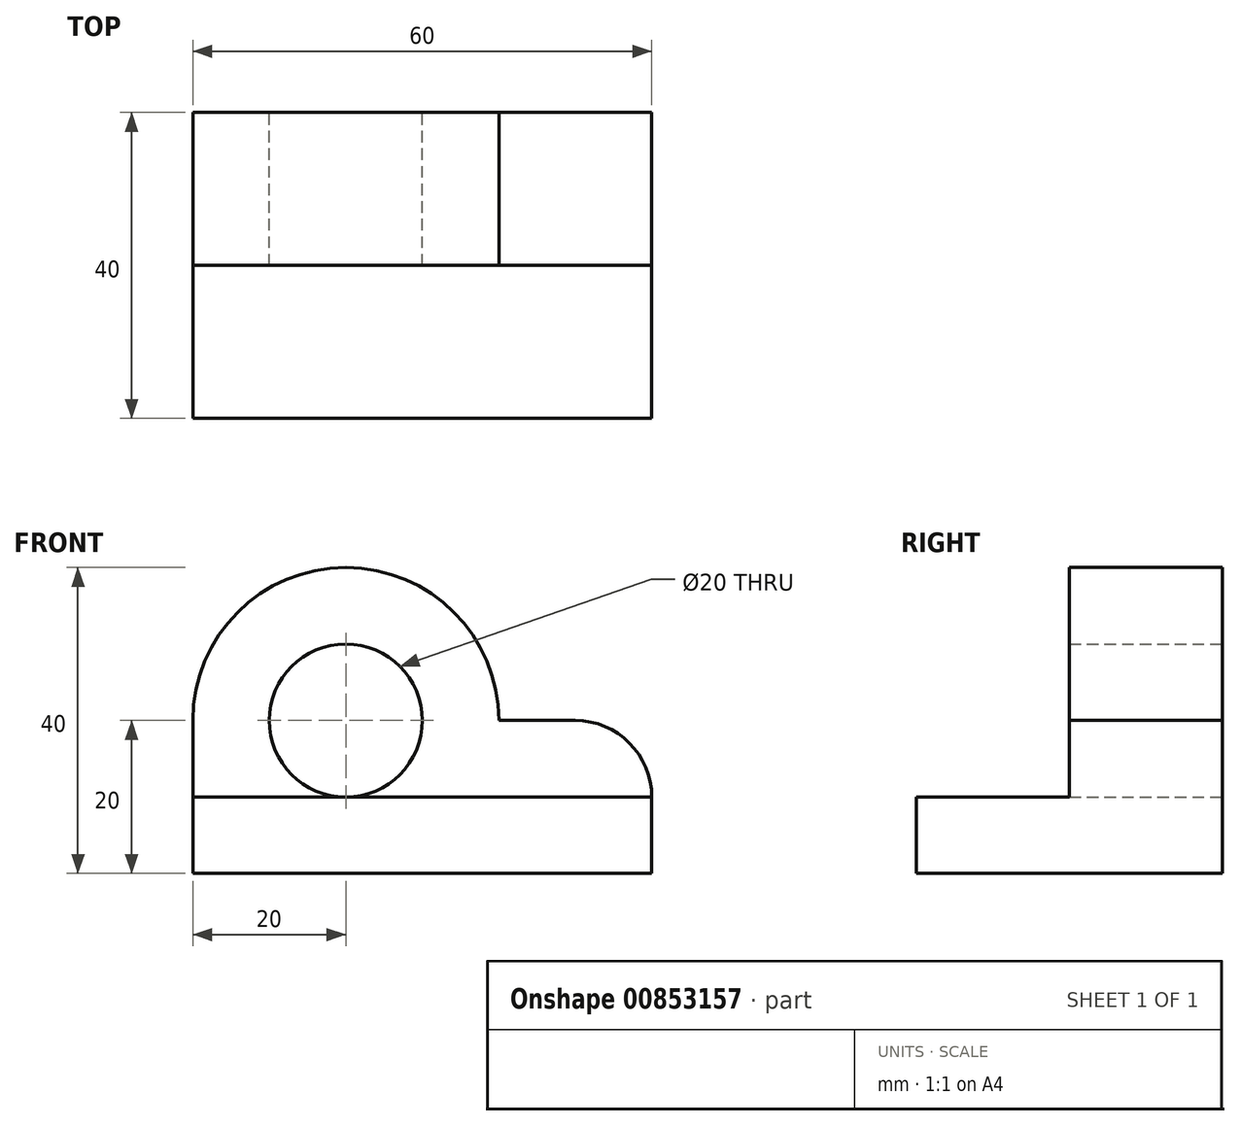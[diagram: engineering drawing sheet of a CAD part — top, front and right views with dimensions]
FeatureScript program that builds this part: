
annotation { "Feature Type Name" : "Feature", "Feature Type Description" : "" }
export const myFeature = defineFeature(function(context is Context, id is Id, definition is map)
    precondition{}
    {
        {
            var Q0;
            Q0=qCreatedBy(makeId("Front.planeOp"),FACE);
            var sketch = newSketch(context, id + "F0", { "sketchPlane" : qUnion([Q0])});
            skLineSegment(sketch, "E0", {"start": v(0, 0) * mm, "end": v(-60, 0) * mm});
            skLineSegment(sketch, "E1", {"start": v(-60, 0) * mm, "end": v(-60, 10) * mm});
            skLineSegment(sketch, "E2", {"start": v(0, 10) * mm, "end": v(0, 0) * mm});
            skArc(sketch, "E3", {"start": v(-20, 20) * mm, "mid": v(-40, 40) * mm, "end": v(-60, 20) * mm});
            skLineSegment(sketch, "E4", {"start": v(-60, 10) * mm, "end": v(-60, 20) * mm});
            skLineSegment(sketch, "E5", {"start": v(0, 10) * mm, "end": v(0, 10) * mm});
            skCircle(sketch, "E6", {"center": v(-40, 20) * mm, "radius": 10 * mm});
            skLineSegment(sketch, "E7", {"start": v(-10, 20) * mm, "end": v(-20, 20) * mm});
            skPoint(sketch, "E8.visualSharp", {"position": v(0, 20) * mm});
            skArc(sketch, "E8.filletArc", {"start": v(0, 10) * mm, "mid": v(-2.93, 17.07) * mm, "end": v(-10, 20) * mm});
            skSolve(sketch);
        }
        {
            var Q0;
            Q0 = qSketchRegion(id + "F0", true);
            extrude(context, id + "F1", {"entities" : qUnion([Q0]), "depth" : 20 * mm, "offsetDistance" : 25 * mm});
        }
        {
            var Q0;
            Q0=makeQuery(id+"F1.opExtrude","CAP_FACE",FACE,{"disambiguationData":[OSD([sQuery(id+"F0.wireOp",EDGE,"E0"),sQuery(id+"F0.wireOp",EDGE,"E1"),sQuery(id+"F0.wireOp",EDGE,"E2"),sQuery(id+"F0.wireOp",EDGE,"E3"),sQuery(id+"F0.wireOp",EDGE,"E4"),sQuery(id+"F0.wireOp",EDGE,"E6"),sQuery(id+"F0.wireOp",EDGE,"E7"),sQuery(id+"F0.wireOp",EDGE,"E8.filletArc")])],"isStart":false});
            var sketch = newSketch(context, id + "F2", { "sketchPlane" : qUnion([Q0])});
            skLineSegment(sketch, "E9.bottom", {"start": v(-60, 0) * mm, "end": v(0, 0) * mm});
            skLineSegment(sketch, "E9.top", {"start": v(-60, 10) * mm, "end": v(0, 10) * mm});
            skLineSegment(sketch, "E9.left", {"start": v(-60, 0) * mm, "end": v(-60, 10) * mm});
            skLineSegment(sketch, "E9.right", {"start": v(0, 0) * mm, "end": v(0, 10) * mm});
            skSolve(sketch);
        }
        {
            var Q0;
            Q0 = qSketchRegion(id + "F2", true);
            extrude(context, id + "F3", {"entities" : qUnion([Q0]), "operationType" : NewBodyOperationType.ADD, "depth" : 20 * mm, "offsetDistance" : 25 * mm});
        }
    });
